# Revit family: Doppelhalter
name_source: partatom
category: HLS-Bauteile
revit_build: Autodesk Revit 2017 (Build: 20190507_1515(x64)
units: mm (PartAtom-declared; Revit-internal decimal feet)

## family parameters
Arbeitsebenenbasiert = Ja
Beim Laden mit Abzugskörper schneiden = Nein
Bemaßung runder Anschluss = Durchmesser verwenden
Gemeinsam genutzt = Ja
Immer vertikal = Nein
Raumberechnungspunkt = Nein
Teiletyp = Normal

## types (4) — shared parameters
Anschluss = M8
B = 16 mm  [stored 0.0524934 ft]
Breite = 16 mm  [stored 0.0524934 ft]
Fabrikat = MEFA
Firma = MEFA Befestigungs- und Montagesysteme GmbH
Höhe = 5 mm
Kurztext1 = Doppelhalter mit Innengewinde
Material = Stahl
Mengeneinheit = St
Vorgabe-Ansicht = 1219 mm
max. zul. Last Zug = 0.20 kN
vpe = 100 St

## per-type parameters (varying)
| type | Achsabstand | Artikelnummer | EAN | Gewicht | Gewicht pro Bauteil | Kurztext2 | L | LG | Länge |
| Doppelhalter, IG M 8, L= 65 LG= 87 | 65 mm | 0763071 | 4250928417367 | 0.04 kg | 0.04 kg | Achsabstand L 65 mm Anschluss M8 | 65 mm  [stored 0.213255 ft] | 87 mm  [stored 0.285433 ft] | 87 mm  [stored 0.285433 ft] |
| Doppelhalter, IG M 8, L= 85 LG=105,5 | 85 mm | 0763098 | 4250928417374 | 0.06 kg | 0.06 kg | Achsabstand L 85 mm Anschluss M8 | 85 mm  [stored 0.278871 ft] | 106 mm | 106 mm |
| Doppelhalter, IG M 8, L=105 LG=125,5 | 105 mm | 0763128 | 4250928417381 | 0.07 kg | 0.07 kg | Achsabstand L 105 mm Anschluss M8 | 105 mm  [stored 0.344488 ft] | 126 mm | 126 mm |
| Doppelhalter, IG M 8, L=160 LG=181 | 160 mm | 0763160 | 4250928417398 | 0.10 kg | 0.10 kg | Achsabstand L 160 mm Anschluss M8 | 160 mm  [stored 0.524934 ft] | 181 mm  [stored 0.593832 ft] | 181 mm  [stored 0.593832 ft] |

note: [stored X ft] marks values corroborated as IEEE doubles in the binary element streams (Revit-internal decimal feet)
